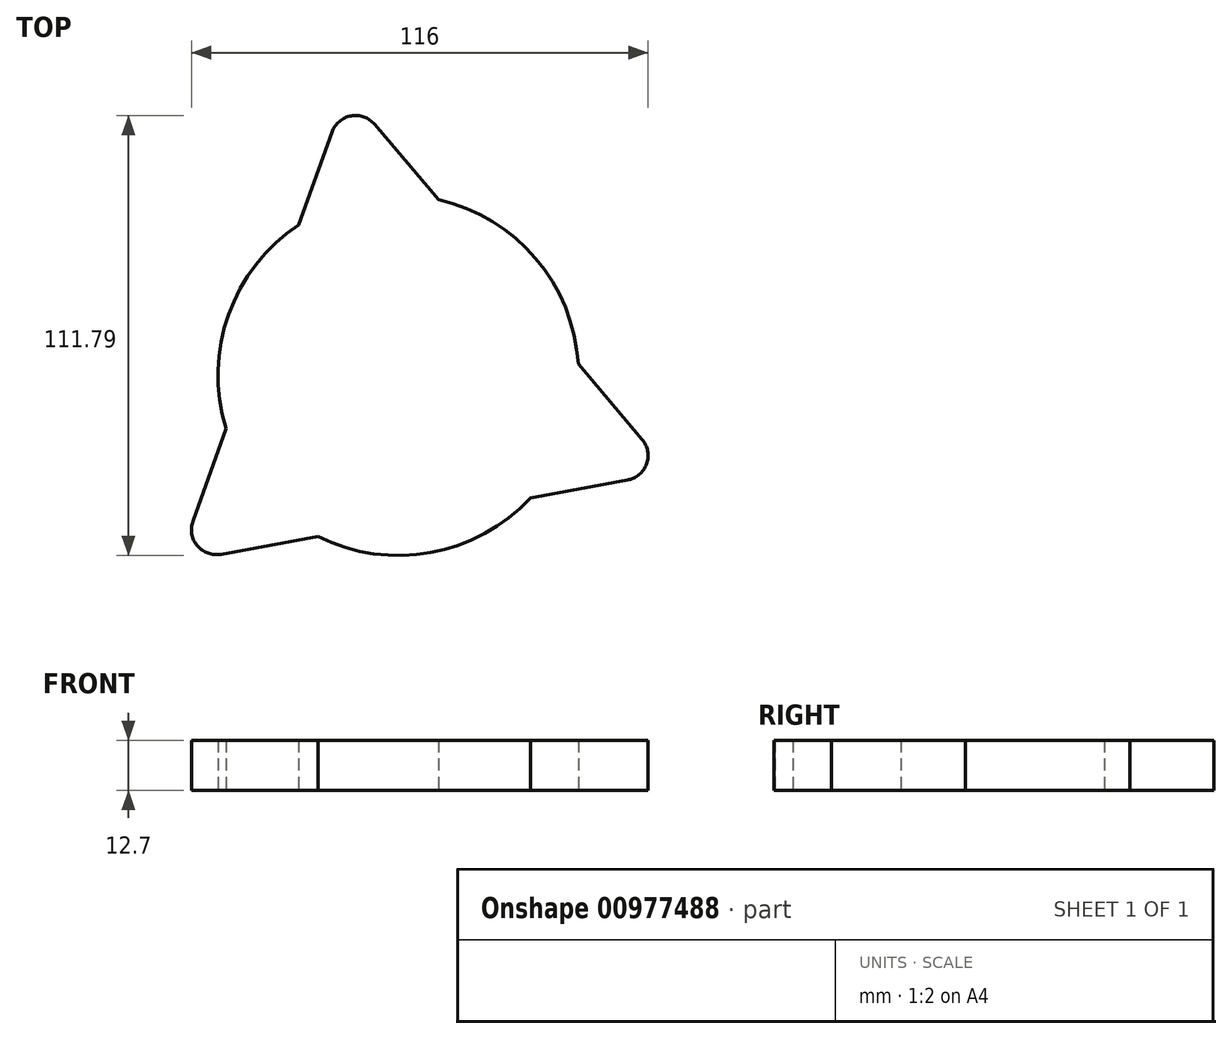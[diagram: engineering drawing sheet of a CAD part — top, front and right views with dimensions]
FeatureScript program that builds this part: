
annotation { "Feature Type Name" : "Feature", "Feature Type Description" : "" }
export const myFeature = defineFeature(function(context is Context, id is Id, definition is map)
    precondition{}
    {
        {
            var Q0;
            Q0=qCreatedBy(makeId("Top.planeOp"),FACE);
            var sketch = newSketch(context, id + "F0", { "sketchPlane" : qUnion([Q0])});
            skCircle(sketch, "E0.cCircle", {"center": v(0, 0) * mm, "radius": 36.66 * mm, "construction": true});
            skLineSegment(sketch, "E0.0", {"start": v(-6.03, 63.75) * mm, "end": v(10.18, 44.66) * mm});
            skLineSegment(sketch, "E0.1", {"start": v(58.23, -26.65) * mm, "end": v(33.59, -31.14) * mm});
            skLineSegment(sketch, "E0.2", {"start": v(-52.2, -37.1) * mm, "end": v(-43.76, -13.51) * mm});
            skPoint(sketch, "E0.0.midPoint", {"position": v(27.95, 23.73) * mm});
            skPoint(sketch, "E1.visualSharp", {"position": v(-13.15, 72.13) * mm});
            skArc(sketch, "E1.filletArc", {"start": v(-6.03, 63.75) * mm, "mid": v(-12.01, 65.89) * mm, "end": v(-16.85, 61.78) * mm});
            skPoint(sketch, "E2.visualSharp", {"position": v(-55.9, -47.46) * mm});
            skArc(sketch, "E2.filletArc", {"start": v(-52.2, -37.1) * mm, "mid": v(-51.05, -43.35) * mm, "end": v(-45.07, -45.48) * mm});
            skPoint(sketch, "E3.visualSharp", {"position": v(69.05, -24.68) * mm});
            skArc(sketch, "E3.filletArc", {"start": v(58.23, -26.65) * mm, "mid": v(63.07, -22.54) * mm, "end": v(61.93, -16.3) * mm});
            skArc(sketch, "E4", {"start": v(-20.43, -41) * mm, "mid": v(8.22, -45.06) * mm, "end": v(33.59, -31.14) * mm});
            skLineSegment(sketch, "E5.trimOffspring", {"start": v(-20.43, -41) * mm, "end": v(-45.07, -45.48) * mm});
            skArc(sketch, "E6.trimOffspring", {"start": v(45.72, 2.8) * mm, "mid": v(34.91, 29.64) * mm, "end": v(10.18, 44.66) * mm});
            skLineSegment(sketch, "E7.trimOffspring", {"start": v(45.72, 2.8) * mm, "end": v(61.93, -16.3) * mm});
            skArc(sketch, "E8.trimOffspring", {"start": v(-25.28, 38.2) * mm, "mid": v(-43.13, 15.41) * mm, "end": v(-43.76, -13.51) * mm});
            skLineSegment(sketch, "E9.trimOffspring", {"start": v(-25.28, 38.2) * mm, "end": v(-16.85, 61.78) * mm});
            skSolve(sketch);
        }
        {
            var Q0;
            Q0 = qSketchRegion(id + "F0", true);
            extrude(context, id + "F1", {"entities" : qUnion([Q0]), "depth" : 12.7 * mm, "offsetDistance" : 25.4 * mm});
        }
    });
